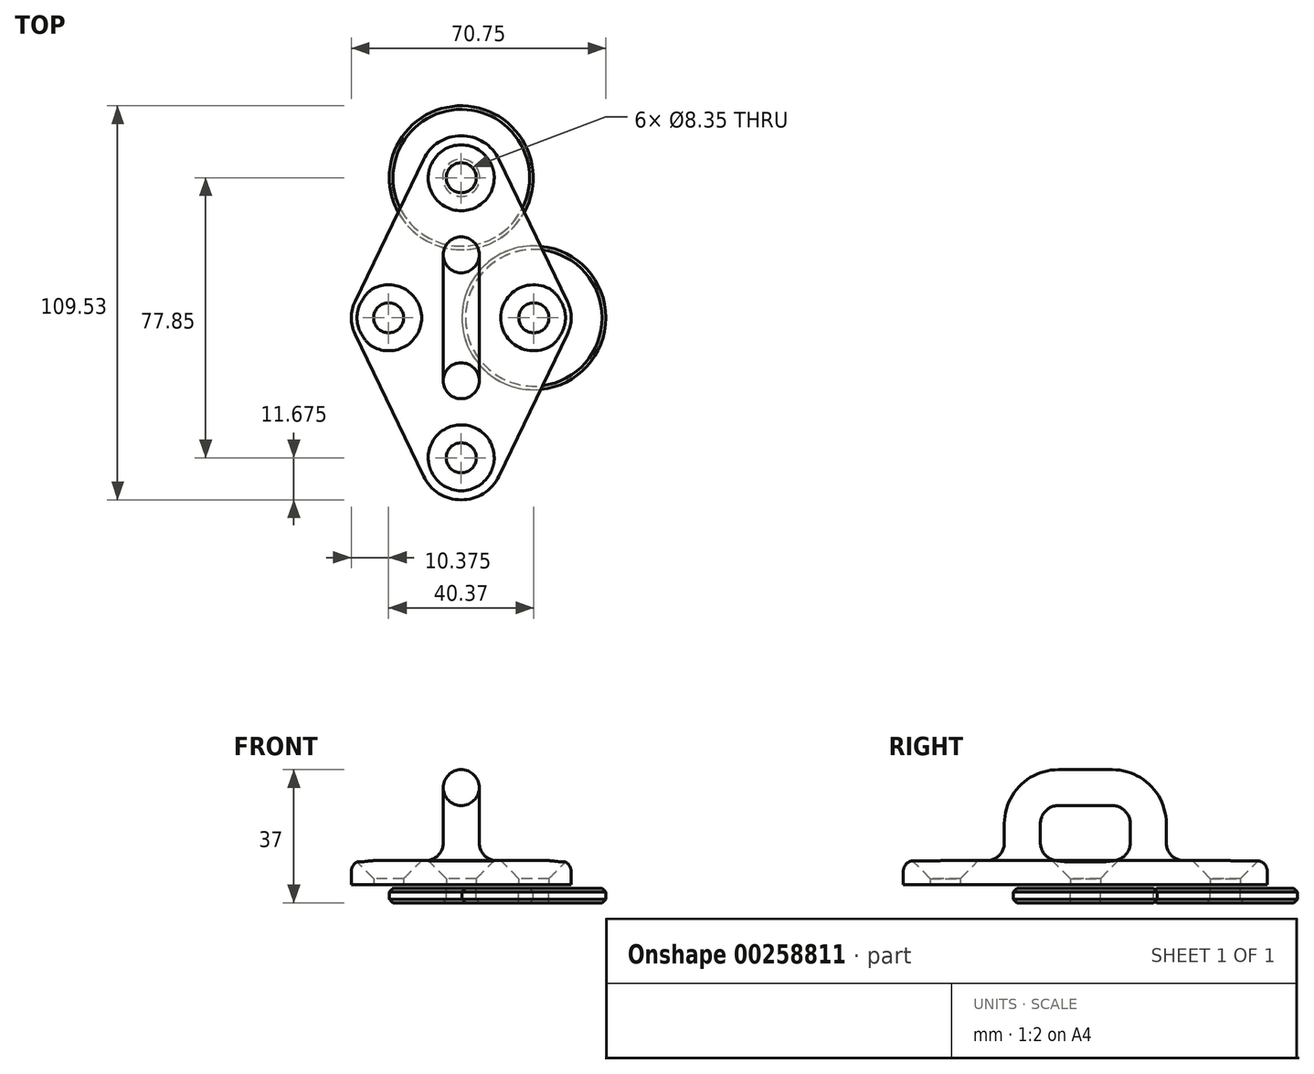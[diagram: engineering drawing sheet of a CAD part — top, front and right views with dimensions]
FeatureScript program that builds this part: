
annotation { "Feature Type Name" : "Feature", "Feature Type Description" : "" }
export const myFeature = defineFeature(function(context is Context, id is Id, definition is map)
    precondition{}
    {
        {
            var Q0;
            Q0=qCreatedBy(makeId("Top.planeOp"),FACE);
            var sketch = newSketch(context, id + "F0", { "sketchPlane" : qUnion([Q0])});
            skCircle(sketch, "E0", {"center": v(-20.18, 0) * mm, "radius": 4.17 * mm});
            skCircle(sketch, "E1", {"center": v(0, 38.93) * mm, "radius": 4.17 * mm});
            skCircle(sketch, "E2.MirrorC", {"center": v(20.18, 0) * mm, "radius": 4.17 * mm});
            skCircle(sketch, "E3.MirrorC", {"center": v(0, -38.93) * mm, "radius": 4.17 * mm});
            skArc(sketch, "E4.0", {"start": v(0, -50.6) * mm, "mid": v(-6.21, -48.81) * mm, "end": v(-10.52, -43.99) * mm});
            skArc(sketch, "E5.0", {"start": v(-30.56, 0) * mm, "mid": v(-30.3, -2.3) * mm, "end": v(-29.53, -4.5) * mm});
            skLineSegment(sketch, "E6", {"start": v(-10.52, -43.99) * mm, "end": v(-29.53, -4.5) * mm});
            skArc(sketch, "E7.MirrorCS", {"start": v(0, -50.6) * mm, "mid": v(6.21, -48.81) * mm, "end": v(10.52, -43.99) * mm});
            skLineSegment(sketch, "E8.MirrorCS", {"start": v(10.52, -43.99) * mm, "end": v(29.53, -4.5) * mm});
            skArc(sketch, "E9.MirrorCS", {"start": v(30.56, 0) * mm, "mid": v(30.3, -2.3) * mm, "end": v(29.53, -4.5) * mm});
            skArc(sketch, "E10.MirrorCS", {"start": v(-30.56, 0) * mm, "mid": v(-30.3, 2.3) * mm, "end": v(-29.53, 4.5) * mm});
            skLineSegment(sketch, "E11.MirrorCS", {"start": v(-10.52, 43.99) * mm, "end": v(-29.53, 4.5) * mm});
            skArc(sketch, "E12.MirrorCS", {"start": v(0, 50.6) * mm, "mid": v(-6.21, 48.81) * mm, "end": v(-10.52, 43.99) * mm});
            skArc(sketch, "E13.MirrorCS", {"start": v(0, 50.6) * mm, "mid": v(6.21, 48.81) * mm, "end": v(10.52, 43.99) * mm});
            skLineSegment(sketch, "E14.MirrorCS", {"start": v(10.52, 43.99) * mm, "end": v(29.53, 4.5) * mm});
            skArc(sketch, "E15.MirrorCS", {"start": v(30.56, 0) * mm, "mid": v(30.3, 2.3) * mm, "end": v(29.53, 4.5) * mm});
            skSolve(sketch);
        }
        {
            var Q0;
            Q0 = qSketchRegion(id + "F0", true);
            extrude(context, id + "F1", {"entities" : qUnion([Q0]), "depth" : 6.7 * mm});
        }
        {
            var Q0;
            Q0=makeQuery(id+"F1.opExtrude","CAP_EDGE",EDGE,{"disambiguationData":[OSD([sQuery(id+"F0.wireOp",EDGE,"E6")])],"isStart":false});
            fillet(context, id + "F2", {"entities" : qUnion([Q0]), "radius" : 3 * mm, "tangentPropagation" : true, "allowEdgeOverflow" : false});
        }
        {
            var Q0;
            Q0=makeQuery(id+"F1.opExtrude","CAP_EDGE",EDGE,{"disambiguationData":[OSD([sQuery(id+"F0.wireOp",EDGE,"E3.MirrorC")])],"isStart":false});
            var Q1;
            Q1=makeQuery(id+"F1.opExtrude","CAP_EDGE",EDGE,{"disambiguationData":[OSD([sQuery(id+"F0.wireOp",EDGE,"E0")])],"isStart":false});
            var Q2;
            Q2=makeQuery(id+"F1.opExtrude","CAP_EDGE",EDGE,{"disambiguationData":[OSD([sQuery(id+"F0.wireOp",EDGE,"E1")])],"isStart":false});
            var Q3;
            Q3=makeQuery(id+"F1.opExtrude","CAP_EDGE",EDGE,{"disambiguationData":[OSD([sQuery(id+"F0.wireOp",EDGE,"E2.MirrorC")])],"isStart":false});
            chamfer(context, id + "F3", {"entities" : qUnion([Q0, Q1, Q2, Q3]), "width" : 5 * mm, "tangentPropagation" : true});
        }
        {
            var Q0;
            Q0=qCreatedBy(makeId("Right.planeOp"),FACE);
            var sketch = newSketch(context, id + "F4", { "sketchPlane" : qUnion([Q0])});
            skLineSegment(sketch, "E16", {"start": v(-17.5, 0) * mm, "end": v(-17.5, 17) * mm});
            skLineSegment(sketch, "E17", {"start": v(-7.5, 27) * mm, "end": v(0, 27) * mm});
            skPoint(sketch, "E18.visualSharp", {"position": v(-17.5, 27) * mm});
            skArc(sketch, "E18.filletArc", {"start": v(-7.5, 27) * mm, "mid": v(-14.57, 24.07) * mm, "end": v(-17.5, 17) * mm});
            skLineSegment(sketch, "E19.MirrorCS", {"start": v(7.5, 27) * mm, "end": v(0, 27) * mm});
            skArc(sketch, "E20.MirrorCS", {"start": v(7.5, 27) * mm, "mid": v(14.57, 24.07) * mm, "end": v(17.5, 17) * mm});
            skLineSegment(sketch, "E21.MirrorCS", {"start": v(17.5, 0) * mm, "end": v(17.5, 17) * mm});
            skSolve(sketch);
        }
        {
            var Q0;
            Q0=qCreatedBy(makeId("Top.planeOp"),FACE);
            var sketch = newSketch(context, id + "F5", { "sketchPlane" : qUnion([Q0])});
            skCircle(sketch, "E22", {"center": v(0, -17.5) * mm, "radius": 5 * mm});
            skSolve(sketch);
        }
        {
            var Q0;
            Q0 = qSketchRegion(id + "F5", true);
            var Q1;
            Q1=sQuery(id+"F4.wireOp",EDGE,"E16");
            var Q2;
            Q2=sQuery(id+"F4.wireOp",EDGE,"E18.filletArc");
            var Q3;
            Q3=sQuery(id+"F4.wireOp",EDGE,"E17");
            var Q4;
            Q4=sQuery(id+"F4.wireOp",EDGE,"E19.MirrorCS");
            var Q5;
            Q5=sQuery(id+"F4.wireOp",EDGE,"E20.MirrorCS");
            var Q6;
            Q6=sQuery(id+"F4.wireOp",EDGE,"E21.MirrorCS");
            sweep(context, id + "F6", {"operationType" : NewBodyOperationType.ADD, "profiles" : qUnion([Q0]), "path" : qUnion([Q1, Q2, Q3, Q4, Q5, Q6])});
        }
        {
            var Q0;
            Q0=makeQuery(id+"F6.boolean.opBoolean","INTERSECT",EDGE,{"derivedFrom":[makeQuery(id+"F1.opExtrude","CAP_FACE",FACE,{"disambiguationData":[OSD([sQuery(id+"F0.wireOp",EDGE,"E0"),sQuery(id+"F0.wireOp",EDGE,"E1"),sQuery(id+"F0.wireOp",EDGE,"E2.MirrorC"),sQuery(id+"F0.wireOp",EDGE,"E3.MirrorC"),sQuery(id+"F0.wireOp",EDGE,"E4.0"),sQuery(id+"F0.wireOp",EDGE,"E5.0"),sQuery(id+"F0.wireOp",EDGE,"E6"),sQuery(id+"F0.wireOp",EDGE,"E7.MirrorCS"),sQuery(id+"F0.wireOp",EDGE,"E8.MirrorCS"),sQuery(id+"F0.wireOp",EDGE,"E9.MirrorCS"),sQuery(id+"F0.wireOp",EDGE,"E10.MirrorCS"),sQuery(id+"F0.wireOp",EDGE,"E11.MirrorCS"),sQuery(id+"F0.wireOp",EDGE,"E12.MirrorCS"),sQuery(id+"F0.wireOp",EDGE,"E13.MirrorCS"),sQuery(id+"F0.wireOp",EDGE,"E14.MirrorCS"),sQuery(id+"F0.wireOp",EDGE,"E15.MirrorCS")])],"isStart":false}),makeQuery(id+"F6.opSweep","SWEPT_FACE",FACE,{"disambiguationData":[OSD([sQuery(id+"F4.wireOp",EDGE,"E16"),sQuery(id+"F5.wireOp",EDGE,"E22")])]})]});
            var Q1;
            Q1=makeQuery(id+"F6.boolean.opBoolean","INTERSECT",EDGE,{"derivedFrom":[makeQuery(id+"F1.opExtrude","CAP_FACE",FACE,{"disambiguationData":[OSD([sQuery(id+"F0.wireOp",EDGE,"E0"),sQuery(id+"F0.wireOp",EDGE,"E1"),sQuery(id+"F0.wireOp",EDGE,"E2.MirrorC"),sQuery(id+"F0.wireOp",EDGE,"E3.MirrorC"),sQuery(id+"F0.wireOp",EDGE,"E4.0"),sQuery(id+"F0.wireOp",EDGE,"E5.0"),sQuery(id+"F0.wireOp",EDGE,"E6"),sQuery(id+"F0.wireOp",EDGE,"E7.MirrorCS"),sQuery(id+"F0.wireOp",EDGE,"E8.MirrorCS"),sQuery(id+"F0.wireOp",EDGE,"E9.MirrorCS"),sQuery(id+"F0.wireOp",EDGE,"E10.MirrorCS"),sQuery(id+"F0.wireOp",EDGE,"E11.MirrorCS"),sQuery(id+"F0.wireOp",EDGE,"E12.MirrorCS"),sQuery(id+"F0.wireOp",EDGE,"E13.MirrorCS"),sQuery(id+"F0.wireOp",EDGE,"E14.MirrorCS"),sQuery(id+"F0.wireOp",EDGE,"E15.MirrorCS")])],"isStart":false}),makeQuery(id+"F6.opSweep","SWEPT_FACE",FACE,{"disambiguationData":[OSD([sQuery(id+"F4.wireOp",EDGE,"E21.MirrorCS"),sQuery(id+"F5.wireOp",EDGE,"E22")])]})]});
            fillet(context, id + "F7", {"entities" : qUnion([Q0, Q1]), "radius" : 5 * mm, "tangentPropagation" : true, "allowEdgeOverflow" : false});
        }
        {
            var Q0;
            Q0=makeQuery(id+"F1.opExtrude","CAP_FACE",FACE,{"disambiguationData":[OSD([sQuery(id+"F0.wireOp",EDGE,"E0"),sQuery(id+"F0.wireOp",EDGE,"E1"),sQuery(id+"F0.wireOp",EDGE,"E2.MirrorC"),sQuery(id+"F0.wireOp",EDGE,"E3.MirrorC"),sQuery(id+"F0.wireOp",EDGE,"E4.0"),sQuery(id+"F0.wireOp",EDGE,"E5.0"),sQuery(id+"F0.wireOp",EDGE,"E6"),sQuery(id+"F0.wireOp",EDGE,"E7.MirrorCS"),sQuery(id+"F0.wireOp",EDGE,"E8.MirrorCS"),sQuery(id+"F0.wireOp",EDGE,"E9.MirrorCS"),sQuery(id+"F0.wireOp",EDGE,"E10.MirrorCS"),sQuery(id+"F0.wireOp",EDGE,"E11.MirrorCS"),sQuery(id+"F0.wireOp",EDGE,"E12.MirrorCS"),sQuery(id+"F0.wireOp",EDGE,"E13.MirrorCS"),sQuery(id+"F0.wireOp",EDGE,"E14.MirrorCS"),sQuery(id+"F0.wireOp",EDGE,"E15.MirrorCS")])],"isStart":true});
            var sketch = newSketch(context, id + "F8", { "sketchPlane" : qUnion([Q0])});
            skCircle(sketch, "E23.0", {"center": v(0, -38.93) * mm, "radius": 4.17 * mm});
            skCircle(sketch, "E24", {"center": v(0, -38.93) * mm, "radius": 20 * mm});
            skCircle(sketch, "E25.0", {"center": v(20.18, 0) * mm, "radius": 4.17 * mm});
            skCircle(sketch, "E26", {"center": v(20.18, 0) * mm, "radius": 20 * mm});
            skSolve(sketch);
        }
        {
            var Q0;
            Q0 = qSketchRegion(id + "F8", true);
            extrude(context, id + "F9", {"entities" : qUnion([Q0]), "depth" : 5 * mm, "offsetDistance" : 25 * mm, "hasSecondDirection" : true, "secondDirectionOppositeDirection" : false, "secondDirectionDepth" : 1 * mm});
        }
        {
            var Q0;
            Q0=makeQuery(id+"F9.opExtrude","CAP_EDGE",EDGE,{"disambiguationData":[OSD([sQuery(id+"F8.wireOp",EDGE,"E26")])],"isStart":false});
            var Q1;
            Q1=makeQuery(id+"F9.opExtrude","CAP_FACE",FACE,{"disambiguationData":[OSD([sQuery(id+"F8.wireOp",EDGE,"E23.0"),sQuery(id+"F8.wireOp",EDGE,"E24")])],"isStart":false});
            var Q2;
            Q2=makeQuery(id+"F9.opExtrude","CAP_EDGE",EDGE,{"disambiguationData":[OSD([sQuery(id+"F8.wireOp",EDGE,"E24")])],"isStart":true});
            var Q3;
            Q3=makeQuery(id+"F9.opExtrude","CAP_EDGE",EDGE,{"disambiguationData":[OSD([sQuery(id+"F8.wireOp",EDGE,"E26")])],"isStart":true});
            chamfer(context, id + "F10", {"entities" : qUnion([Q0, Q1, Q2, Q3]), "width" : 1 * mm, "tangentPropagation" : true});
        }
    });
